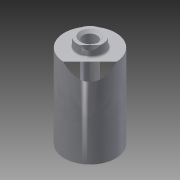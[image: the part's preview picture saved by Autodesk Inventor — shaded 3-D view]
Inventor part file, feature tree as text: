
AUTODESK INVENTOR PART (.ipt)
format: ipt  version: 2014 (Build 180170000, 170)  size: 142,336 bytes
history: native  units: mm
features: extrude x7, sketch x7, chamfer x2, fillet x1, reference x1
ambient origin geometry x8: Origin, YZ Plane, XZ Plane, XY Plane, X Axis, Y Axis, Z Axis, Center Point
bodies: Solid1 (feature_tree)
feature tree (18):
  extrude  "Extrusion1"  Depth=4.0mm
  extrude  "Extrusion2"  Depth=1.5mm
  extrude  "Extrusion3"  Depth=0.5mm TaperAngle=0.0deg
  extrude  "Extrusion4"  Depth=1.0mm TaperAngle=0.0deg
  extrude  "Extrusion5"  Depth=2.0mm
  extrude  "Extrusion6"  Depth=0.3mm
  chamfer  "Chamfer2"  Distance=2.0mm Angle=45.0deg
  extrude  "Extrusion7"  [1 undecoded]
  fillet  "Fillet1"  [1 undecoded]
  chamfer  "Chamfer3"  [1 undecoded]
  sketch  "Sketch1"  dims[d0=13.0mm d1=0.0mm d5=4.0mm]
  reference  "Reference1"
  sketch  "Sketch2"  dims[d6=1.5mm d7=0.0mm d8=2.1mm]
  sketch  "Sketch3"  dims[d9=20.0mm d10=0.0mm d11=0.5mm d12=0.0mm]
  sketch  "Sketch4"  dims[d13=0.5mm d14=0.0mm d15=1.0mm d16=0.0mm]
  sketch  "Sketch5"  dims[d17=0.2mm d18=2.0mm d19=45.0deg d20=2.2mm]
  sketch  "Sketch6"  dims[d21=30.0mm d22=0.0mm d23=0.3mm d24=0.4mm d25=2.0mm d26=45.0deg]
  sketch  "Sketch7"
note: 3 required parameter values undecoded (feature->parameter linkage not recoverable at this tier; creation-order binding heuristic only, values carry confidence <= 0.55)
